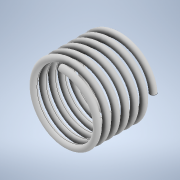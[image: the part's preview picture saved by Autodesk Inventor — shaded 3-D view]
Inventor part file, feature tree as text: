
AUTODESK INVENTOR PART (.ipt)
format: ipt  version: 2022 (Build 260153000, 153)  size: 330,240 bytes
history: native  units: in
note: dims shown in document units (in); Inventor stores cm internally (conversion verified against a paired STEP export)
features: helix x1, sketch x1
ambient origin geometry x8: Origin, YZ Plane, XZ Plane, XY Plane, X Axis, Y Axis, Z Axis, Center Point
bodies: Solid1 (feature_tree)
feature tree (2):
  helix  "Coil1"  [1 undecoded]
  sketch  "Sketch2"  dims[d1=0.1969in d2=0.1083in d3=0.0295in d4=1.0in d5=2.4606in d6=0.0in d7=90.0deg d8=90.0deg d9=0.0in d10=0.0in]
note: 1 required parameter value undecoded (feature->parameter linkage not recoverable at this tier; creation-order binding heuristic only, values carry confidence <= 0.55)
